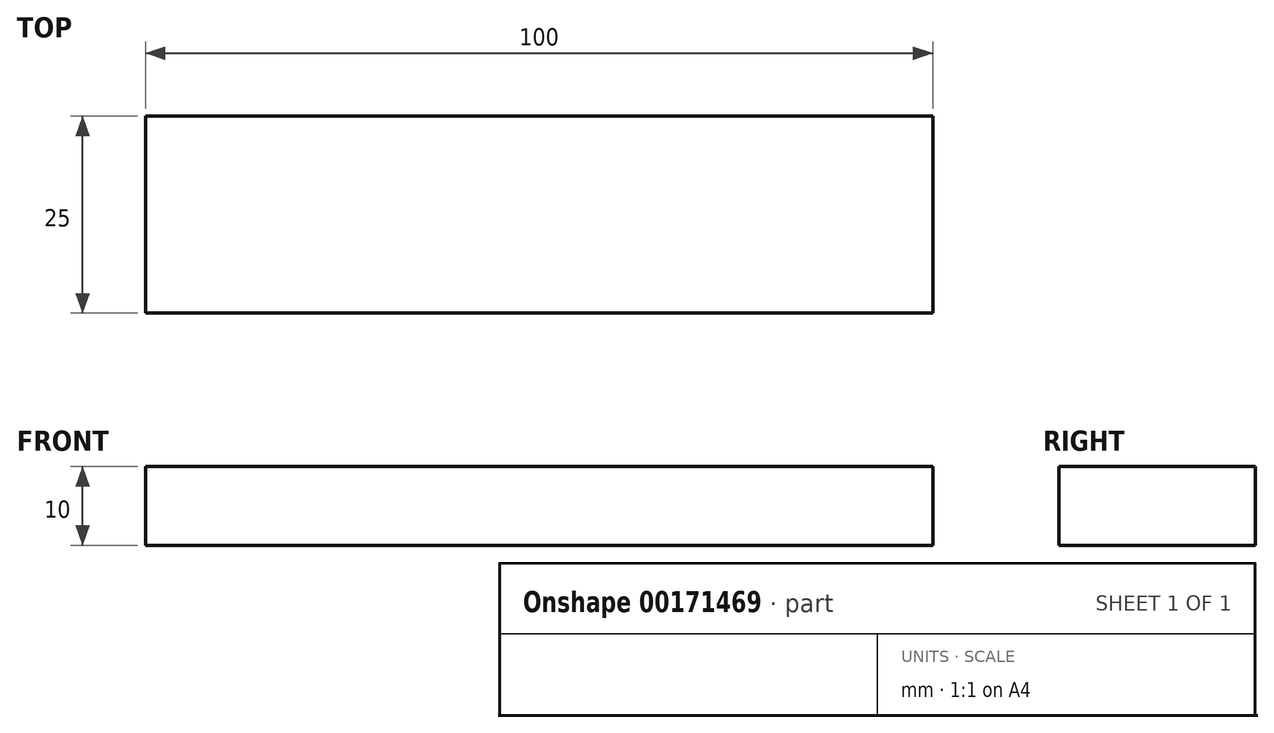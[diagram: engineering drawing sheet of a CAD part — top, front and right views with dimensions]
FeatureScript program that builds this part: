
annotation { "Feature Type Name" : "Feature", "Feature Type Description" : "" }
export const myFeature = defineFeature(function(context is Context, id is Id, definition is map)
    precondition{}
    {
        {
            var Q0;
            Q0=qCreatedBy(makeId("Front.planeOp"),FACE);
            var sketch = newSketch(context, id + "F0", { "sketchPlane" : qUnion([Q0])});
            skLineSegment(sketch, "E0.bottom", {"start": v(0, 0) * mm, "end": v(100, 0) * mm});
            skLineSegment(sketch, "E0.top", {"start": v(0, 10) * mm, "end": v(100, 10) * mm});
            skLineSegment(sketch, "E0.left", {"start": v(0, 0) * mm, "end": v(0, 10) * mm});
            skLineSegment(sketch, "E0.right", {"start": v(100, 0) * mm, "end": v(100, 10) * mm});
            skSolve(sketch);
        }
        {
            var Q0;
            Q0 = qSketchRegion(id + "F0", true);
            extrude(context, id + "F1", {"entities" : qUnion([Q0]), "depth" : 25 * mm});
        }
    });
